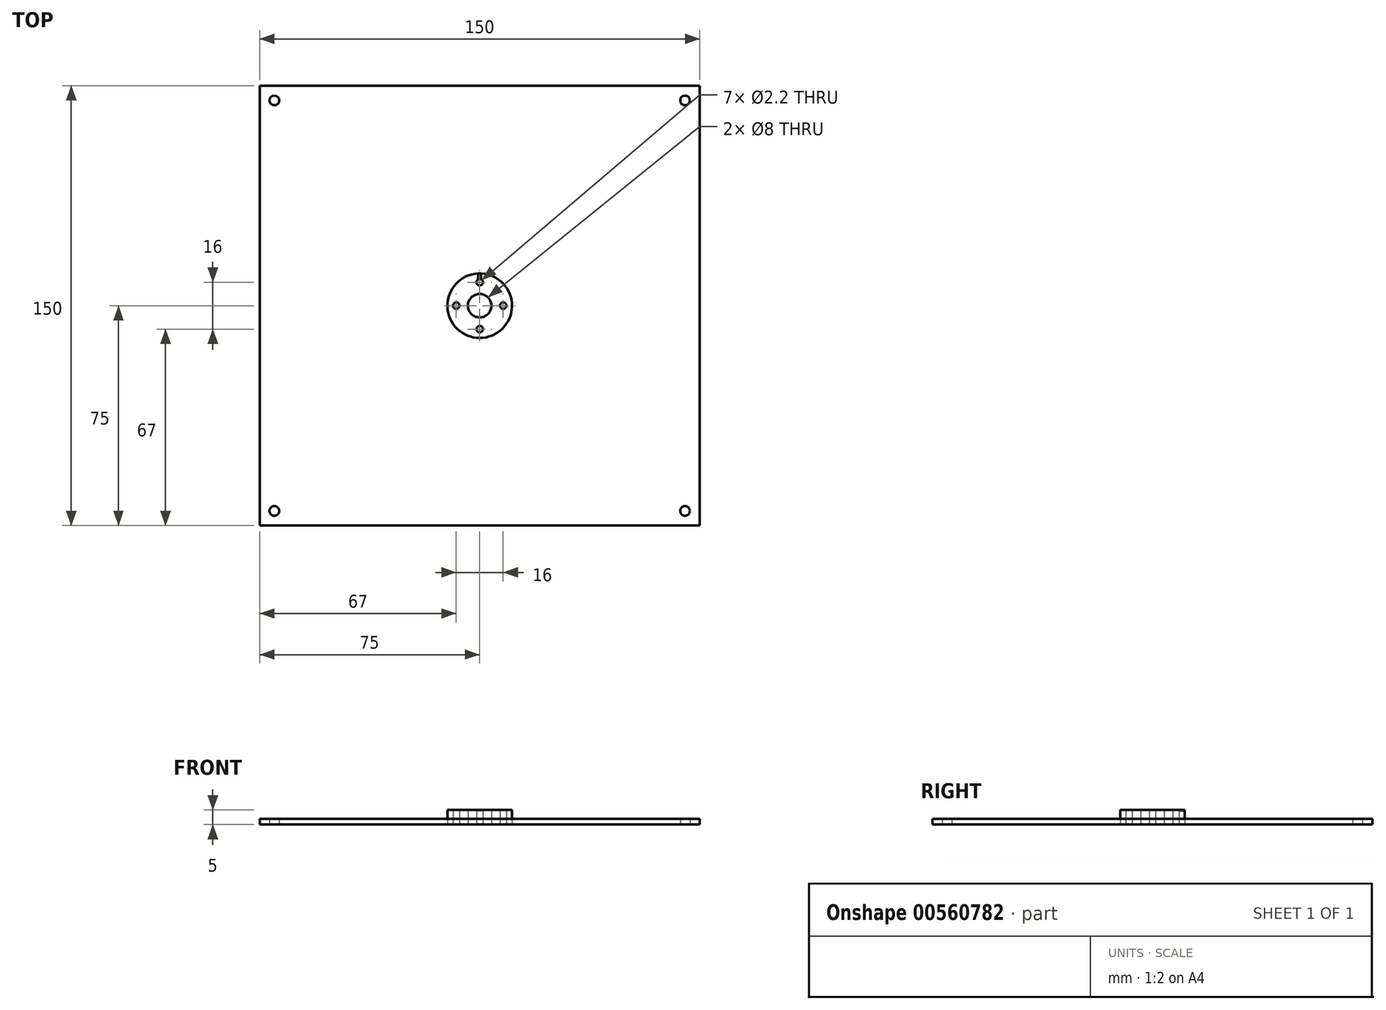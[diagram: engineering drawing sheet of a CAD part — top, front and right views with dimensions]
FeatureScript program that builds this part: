
annotation { "Feature Type Name" : "Feature", "Feature Type Description" : "" }
export const myFeature = defineFeature(function(context is Context, id is Id, definition is map)
    precondition{}
    {
        {
            var Q0;
            Q0=qCreatedBy(makeId("Top.planeOp"),FACE);
            var sketch = newSketch(context, id + "F0", { "sketchPlane" : qUnion([Q0])});
            skCircle(sketch, "E0.cCircle", {"center": v(0, 0) * mm, "radius": 75 * mm, "construction": true});
            skLineSegment(sketch, "E0.0", {"start": v(-75, 75) * mm, "end": v(75, 75) * mm});
            skLineSegment(sketch, "E0.1", {"start": v(75, 75) * mm, "end": v(75, -75) * mm});
            skLineSegment(sketch, "E0.2", {"start": v(75, -75) * mm, "end": v(-75, -75) * mm});
            skLineSegment(sketch, "E0.3", {"start": v(-75, -75) * mm, "end": v(-75, 75) * mm});
            skPoint(sketch, "E0.0.midPoint", {"position": v(0, 75) * mm});
            skCircle(sketch, "E1", {"center": v(0, 0) * mm, "radius": 8 * mm, "construction": true});
            skPoint(sketch, "E2", {"position": v(0, 8) * mm});
            skPoint(sketch, "E3", {"position": v(0, -8) * mm});
            skPoint(sketch, "E4", {"position": v(8, 0) * mm});
            skPoint(sketch, "E5", {"position": v(-8, 0) * mm});
            skCircle(sketch, "E6", {"center": v(0, 0) * mm, "radius": 4 * mm});
            skPoint(sketch, "E7", {"position": v(-70, 70) * mm});
            skPoint(sketch, "E8", {"position": v(70, 70) * mm});
            skPoint(sketch, "E9", {"position": v(70, -70) * mm});
            skPoint(sketch, "E10", {"position": v(-70, -70) * mm});
            skSolve(sketch);
        }
        {
            var Q0;
            Q0=qSketchRegion(id+"F0",true);
            extrude(context, id + "F1", {"entities" : qUnion([Q0]), "depth" : 2 * mm});
        }
        {
            var Q0;
            Q0=sQuery(id+"F0.wireOp",VERTEX,"E2");
            var Q1;
            Q1=sQuery(id+"F0.wireOp",VERTEX,"E5");
            var Q2;
            Q2=sQuery(id+"F0.wireOp",VERTEX,"E3");
            var Q3;
            Q3=sQuery(id+"F0.wireOp",VERTEX,"E4");
            var Q4;
            Q4=makeQuery(id+"F1.opExtrude","SWEPT_BODY",BODY,{"disambiguationData":[OSD([sQuery(id+"F0.wireOp",EDGE,"E0.0"),sQuery(id+"F0.wireOp",EDGE,"E0.1"),sQuery(id+"F0.wireOp",EDGE,"E0.2"),sQuery(id+"F0.wireOp",EDGE,"E0.3")])]});
            hole(context, id + "F2", {"style" : HoleStyle.SIMPLE, "endStyle" : HoleEndStyle.THROUGH, "oppositeDirection" : true, "holeDiameter" : 2.2 * mm, "isTappedThrough" : true, "tappedDepth" : 6.2 * mm, "tapClearance" : 3, "locations" : qUnion([Q0, Q1, Q2, Q3]), "scope" : qUnion([Q4])});
        }
        {
            var Q0;
            Q0=sQuery(id+"F0.wireOp",VERTEX,"E7");
            var Q1;
            Q1=sQuery(id+"F0.wireOp",VERTEX,"E10");
            var Q2;
            Q2=sQuery(id+"F0.wireOp",VERTEX,"E9");
            var Q3;
            Q3=sQuery(id+"F0.wireOp",VERTEX,"E8");
            var Q4;
            Q4=makeQuery(id+"F1.opExtrude","SWEPT_BODY",BODY,{"disambiguationData":[OSD([sQuery(id+"F0.wireOp",EDGE,"E0.0"),sQuery(id+"F0.wireOp",EDGE,"E0.1"),sQuery(id+"F0.wireOp",EDGE,"E0.2"),sQuery(id+"F0.wireOp",EDGE,"E0.3"),sQuery(id+"F0.wireOp",EDGE,"E6")])]});
            hole(context, id + "F3", {"style" : HoleStyle.SIMPLE, "endStyle" : HoleEndStyle.THROUGH, "oppositeDirection" : true, "standardTappedOrClearance" : lookupTablePath({ "standard" : "ISO", "fit" : "Normal", "size" : "M3", "type" : "Clearance" }), "standardBlindInLast" : lookupTablePath({ "fit" : "Standard", "standard" : "ISO", "size" : "M3", "type" : "Clearance" }), "holeDiameter" : 3.3 * mm, "isTappedThrough" : true, "tappedDepth" : 6.2 * mm, "tapClearance" : 3, "locations" : qUnion([Q0, Q1, Q2, Q3]), "scope" : qUnion([Q4])});
        }
        {
            var Q0;
            Q0=qCreatedBy(makeId("Top.planeOp"),FACE);
            var sketch = newSketch(context, id + "F4", { "sketchPlane" : qUnion([Q0])});
            skCircle(sketch, "E11", {"center": v(0, 0) * mm, "radius": 11 * mm});
            skCircle(sketch, "E12", {"center": v(0, 0) * mm, "radius": 8 * mm, "construction": true});
            skPoint(sketch, "E13", {"position": v(0, 8) * mm});
            skPoint(sketch, "E14", {"position": v(-8, 0) * mm});
            skPoint(sketch, "E15", {"position": v(0, -8) * mm});
            skPoint(sketch, "E16", {"position": v(8, 0) * mm});
            skCircle(sketch, "E17", {"center": v(0, 0) * mm, "radius": 4 * mm});
            skSolve(sketch);
        }
        {
            var Q0;
            Q0=qSketchRegion(id+"F4",true);
            extrude(context, id + "F5", {"entities" : qUnion([Q0]), "depth" : 5 * mm});
        }
        {
            var Q0;
            Q0=sQuery(id+"F4.wireOp",VERTEX,"E15");
            var Q1;
            Q1=sQuery(id+"F4.wireOp",VERTEX,"E16");
            var Q2;
            Q2=sQuery(id+"F4.wireOp",VERTEX,"E13");
            var Q3;
            Q3=sQuery(id+"F4.wireOp",VERTEX,"E14");
            var Q4;
            Q4=makeQuery(id+"F5.opExtrude","SWEPT_BODY",BODY,{"disambiguationData":[OSD([sQuery(id+"F4.wireOp",EDGE,"E11")])]});
            hole(context, id + "F6", {"style" : HoleStyle.SIMPLE, "endStyle" : HoleEndStyle.THROUGH, "oppositeDirection" : true, "holeDiameter" : 2.2 * mm, "isTappedThrough" : true, "tappedDepth" : 6.2 * mm, "tapClearance" : 3, "locations" : qUnion([Q0, Q1, Q2, Q3]), "scope" : qUnion([Q4])});
        }
        {
            var Q0;
            Q0=makeQuery(id+"F5.opExtrude","CAP_FACE",FACE,{"disambiguationData":[OSD([sQuery(id+"F4.wireOp",EDGE,"E11"),sQuery(id+"F4.wireOp",EDGE,"E17")])],"isStart":false});
            var sketch = newSketch(context, id + "F7", { "sketchPlane" : qUnion([Q0])});
            skLineSegment(sketch, "E18", {"start": v(0, 0) * mm, "end": v(0, 11) * mm, "construction": true});
            skLineSegment(sketch, "E19", {"start": v(-0.5, 8.98) * mm, "end": v(-0.5, 11) * mm});
            skLineSegment(sketch, "E20", {"start": v(0.5, 10.99) * mm, "end": v(0.5, 8.98) * mm});
            skSolve(sketch);
        }
        {
            var Q0;
            {var subQ6=sQuery(id+"F7.wireOp",EDGE,"E20");Q0=makeQuery(id+"F7.imprint","IMPRINT",FACE,{"disambiguationData":[TD([[makeQuery(id+"F7.imprint","IMPRINT",EDGE,{"derivedFrom":subQ6}),-1.0]])]});}
            extrude(context, id + "F8", {"entities" : qUnion([Q0]), "operationType" : NewBodyOperationType.REMOVE, "oppositeDirection" : true, "depth" : 0.4 * mm});
        }
    });
